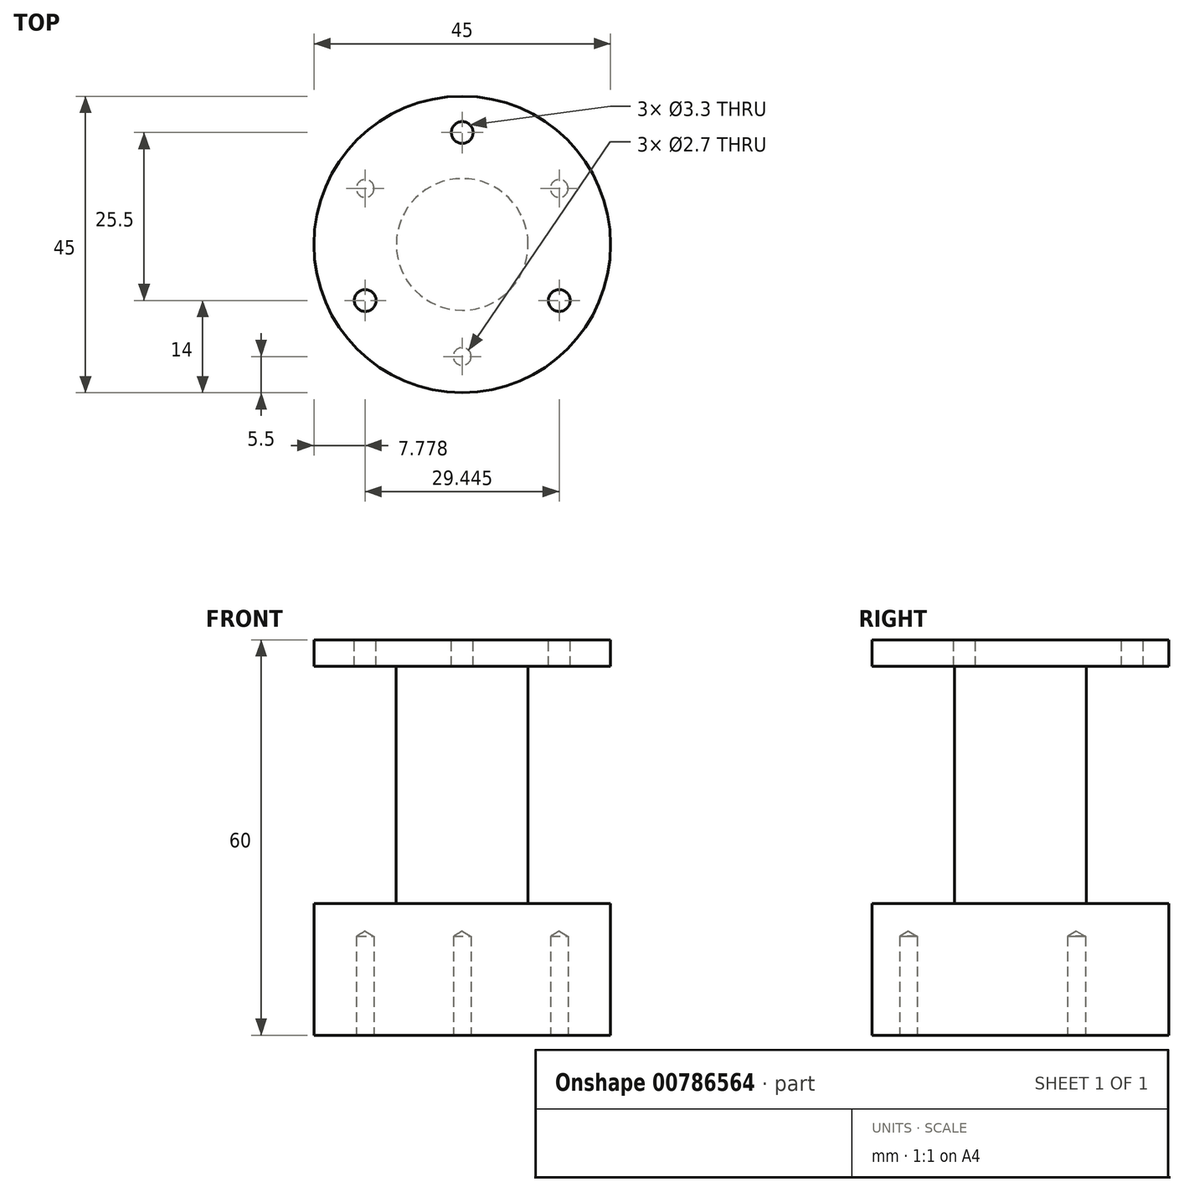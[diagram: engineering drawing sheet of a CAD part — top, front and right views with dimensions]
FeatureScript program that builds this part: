
annotation { "Feature Type Name" : "Feature", "Feature Type Description" : "" }
export const myFeature = defineFeature(function(context is Context, id is Id, definition is map)
    precondition{}
    {
        {
            var Q0;
            Q0=qCreatedBy(makeId("Top.planeOp"),FACE);
            var sketch = newSketch(context, id + "F0", { "sketchPlane" : qUnion([Q0])});
            skCircle(sketch, "E0", {"center": v(0, 0) * mm, "radius": 22.5 * mm});
            skLineSegment(sketch, "E1", {"start": v(0, 0) * mm, "end": v(-38.27, 0) * mm});
            skSolve(sketch);
        }
        {
            var Q0;
            Q0 = qSketchRegion(id + "F0", true);
            extrude(context, id + "F1", {"entities" : qUnion([Q0]), "depth" : 20 * mm, "offsetDistance" : 25 * mm});
        }
        {
            var Q0;
            Q0=makeQuery(id+"F1.opExtrude","CAP_FACE",FACE,{"disambiguationData":[OSD([sQuery(id+"F0.wireOp",EDGE,"E0")])],"isStart":false});
            var sketch = newSketch(context, id + "F2", { "sketchPlane" : qUnion([Q0])});
            skCircle(sketch, "E2", {"center": v(0, 0) * mm, "radius": 10 * mm});
            skSolve(sketch);
        }
        {
            var Q0;
            Q0=makeQuery(id+"F2.imprint","IMPRINT",FACE,{"disambiguationData":[TD([[makeQuery(id+"F2.imprint","IMPRINT",EDGE,{"derivedFrom":sQuery(id+"F2.wireOp",EDGE,"E2")}),1.0]])]});
            extrude(context, id + "F3", {"entities" : qUnion([Q0]), "operationType" : NewBodyOperationType.ADD, "depth" : 36 * mm, "offsetDistance" : 25 * mm});
        }
        {
            var Q0;
            Q0=makeQuery(id+"F3.opExtrude","CAP_FACE",FACE,{"disambiguationData":[OSD([sQuery(id+"F2.wireOp",EDGE,"E2")])],"isStart":false});
            var sketch = newSketch(context, id + "F4", { "sketchPlane" : qUnion([Q0])});
            skCircle(sketch, "E3", {"center": v(0, 0) * mm, "radius": 22.5 * mm});
            skSolve(sketch);
        }
        {
            var Q0;
            Q0=makeQuery(id+"F4.imprint","IMPRINT",FACE,{"disambiguationData":[TD([[makeQuery(id+"F4.imprint","IMPRINT",EDGE,{"derivedFrom":sQuery(id+"F4.wireOp",EDGE,"E3")}),1.0]])]});
            var Q1;
            Q1=makeQuery(id+"F4.imprint","IMPRINT",FACE,{"disambiguationData":[TD([[makeQuery(id+"F4.imprint","IMPRINT",EDGE,{"derivedFrom":makeQuery(id+"F3.opExtrude","CAP_EDGE",EDGE,{"disambiguationData":[OSD([sQuery(id+"F2.wireOp",EDGE,"E2")])],"isStart":false})}),1.0]])]});
            extrude(context, id + "F5", {"entities" : qUnion([Q0, Q1]), "operationType" : NewBodyOperationType.ADD, "depth" : 4 * mm, "offsetDistance" : 25 * mm});
        }
        {
            var Q0;
            Q0=makeQuery(id+"F5.opExtrude","CAP_FACE",FACE,{"disambiguationData":[OSD([sQuery(id+"F4.wireOp",EDGE,"E3")])],"isStart":false});
            var sketch = newSketch(context, id + "F6", { "sketchPlane" : qUnion([Q0])});
            skPoint(sketch, "E4", {"position": v(0, 17) * mm});
            skPoint(sketch, "E5.1.0", {"position": v(-14.72, -8.5) * mm});
            skPoint(sketch, "E5.2.0", {"position": v(14.72, -8.5) * mm});
            skPoint(sketch, "E5.center", {"position": v(0, 0) * mm});
            skSolve(sketch);
        }
        {
            var Q0;
            Q0=sQuery(id+"F6.wireOp",VERTEX,"E4");
            var Q1;
            Q1=sQuery(id+"F6.wireOp",VERTEX,"E5.2.0");
            var Q2;
            Q2=sQuery(id+"F6.wireOp",VERTEX,"E5.1.0");
            var Q3;
            Q3=makeQuery(id+"F1.opExtrude","SWEPT_BODY",BODY,{"disambiguationData":[OSD([sQuery(id+"F0.wireOp",EDGE,"E0")])]});
            hole(context, id + "F7", {"style" : HoleStyle.SIMPLE, "endStyle" : HoleEndStyle.BLIND, "holeDiameter" : 3.3 * mm, "majorDiameter" : 5 * mm, "holeDepth" : 10 * mm, "isTappedThrough" : true, "tappedDepth" : 12 * mm, "tapClearance" : 3, "locations" : qUnion([Q0, Q1, Q2]), "scope" : qUnion([Q3])});
        }
        {
            var Q0;
            Q0=makeQuery(id+"F1.opExtrude","CAP_FACE",FACE,{"disambiguationData":[OSD([sQuery(id+"F0.wireOp",EDGE,"E0")])],"isStart":true});
            var sketch = newSketch(context, id + "F8", { "sketchPlane" : qUnion([Q0])});
            skPoint(sketch, "E6", {"position": v(0, 17) * mm});
            skPoint(sketch, "E7.1.0", {"position": v(-14.72, -8.5) * mm});
            skPoint(sketch, "E7.2.0", {"position": v(14.72, -8.5) * mm});
            skPoint(sketch, "E7.center", {"position": v(0, 0) * mm});
            skSolve(sketch);
        }
        {
            var Q0;
            Q0=sQuery(id+"F8.wireOp",VERTEX,"E7.2.0");
            var Q1;
            Q1=sQuery(id+"F8.wireOp",VERTEX,"E7.1.0");
            var Q2;
            Q2=sQuery(id+"F8.wireOp",VERTEX,"E6");
            var Q3;
            Q3=makeQuery(id+"F1.opExtrude","SWEPT_BODY",BODY,{"disambiguationData":[OSD([sQuery(id+"F0.wireOp",EDGE,"E0")])]});
            hole(context, id + "F9", {"style" : HoleStyle.SIMPLE, "endStyle" : HoleEndStyle.BLIND, "holeDiameter" : 2.7 * mm, "majorDiameter" : 5 * mm, "holeDepth" : 15 * mm, "isTappedThrough" : true, "tappedDepth" : 12 * mm, "tapClearance" : 3, "locations" : qUnion([Q0, Q1, Q2]), "scope" : qUnion([Q3])});
        }
    });
